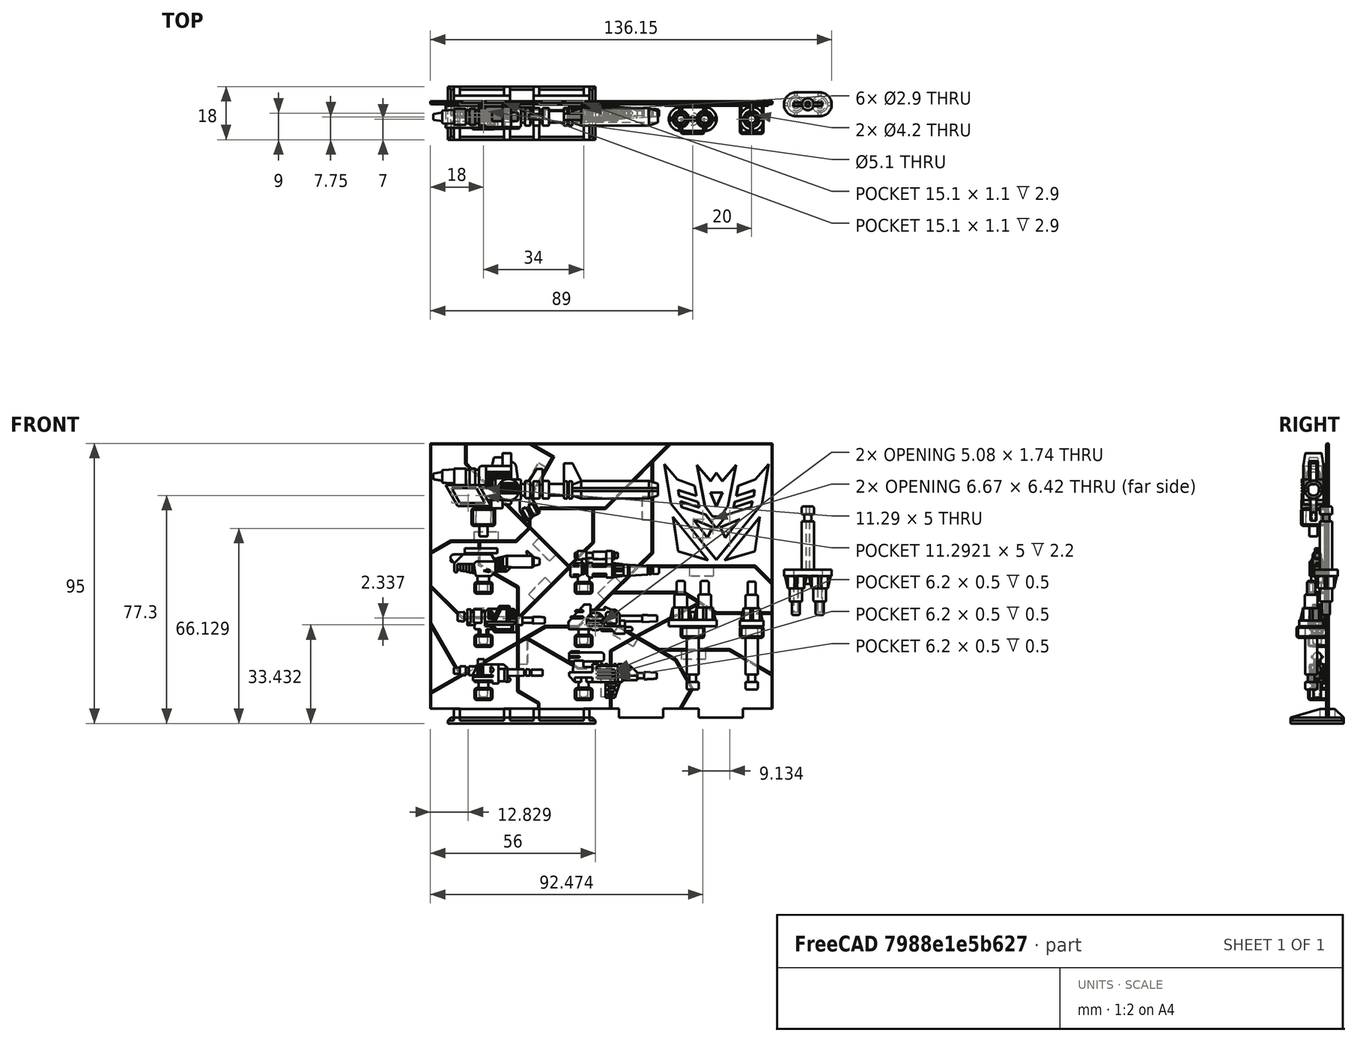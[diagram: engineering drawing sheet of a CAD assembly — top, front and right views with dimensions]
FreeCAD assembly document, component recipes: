
FREECAD ASSEMBLY — COMPONENT RECIPES ("Accesories")

This assembly document has 10 components, labeled P0..P9 below (a component is one placed body or linked part). 9 of them carry a construction recipe — the FreeCAD feature program that regenerates the part from scratch, quoted from this document or its linked companion documents; the rest are supplied as boundary geometry only. No exploded tour is included for this assembly.
NOTE — document 3 of 3 of this assembly tour. The two overview renders and the header above are repeated from document 1; the component sections below continue where the previous document stopped.
COMPONENT P8 — recipe-attached ("Scavanger_Gun", modeled in this document).
Construction recipe (the document's own serialized feature program — sketch geometry with constraints, then the solid features built on it; lengths are millimeters unless a unit is written):

FEATURE [Sketcher::SketchObject] Sketch357
  ArcFitTolerance = 1e-06
  AttachmentOffset = pos=(-22,-37,0) rot=(0,0,1;0rad)
  AttachmentSupport = -> [XZ_Plane027]
  FullyConstrained = true
  MakeInternals = false
  MapMode = 5
  Placement = pos=(-22,-8.2e-15,-37) rot=(1,0,0;1.5708rad)
  sketch-geometry (5):
    g0: LineSegment StartX=-1.6 StartY=-3 StartZ=0 EndX=7 EndY=-3 EndZ=0
    g1: LineSegment StartX=7 StartY=-3 StartZ=0 EndX=7 EndY=3.5 EndZ=0
    g2: LineSegment StartX=7 StartY=3.5 StartZ=0 EndX=0 EndY=3.5 EndZ=0
    g3: LineSegment StartX=0 StartY=3.5 StartZ=0 EndX=-1.6 EndY=0 EndZ=0
    g4: LineSegment StartX=-1.6 StartY=0 StartZ=0 EndX=-1.6 EndY=-3 EndZ=0
  constraints (15):
    c: Horizontal(g0)
    c: Coincident(g1,g0)
    c: Vertical(g1)
    c: Coincident(g2,g1)
    c: Horizontal(g2)
    c: Coincident(g3,g2)
    c: Coincident(g4,g3)
    c: Vertical(g4)
    c: Coincident(g0,g4)
    c: DistanceX(g0,g0) = 8.6
    c: PointOnObject(g2,g-2)
    c: DistanceY(g1,g1) = 6.5
    c: DistanceX(g2,g2) = 7
    c: DistanceY(g4,g4) = 3
    c: PointOnObject(g3,g-1)
FEATURE [PartDesign::Pad] Pad234
  Direction = (0,-1,2e-16)
  Length = 5
  Length2 = 10
  Placement = pos=(0,0,0) rot=(1,0,0;1.5708rad)
  Profile = -> Sketch357
  ReferenceAxis = -> Sketch357 [N_Axis]
  Refine = true
  Suppressed = false
  Type = 0
FEATURE [Sketcher::SketchObject] Sketch358
  ArcFitTolerance = 1e-06
  AttachmentSupport = -> [Pad234]
  ExternalGeometry = -> [Pad234]
  FullyConstrained = true
  MakeInternals = false
  MapMode = 5
  Placement = pos=(0,-1.76e-14,-40) rot=(1,0,0;3.14159rad)
  sketch-geometry (8):
    g0: LineSegment StartX=-17.1 StartY=5 StartZ=0 EndX=-17.1 EndY=4.5 EndZ=0
    g1: LineSegment StartX=-17.1 StartY=4.5 StartZ=0 EndX=-23.1 EndY=4.5 EndZ=0
    g2: LineSegment StartX=-23.1 StartY=4.5 StartZ=0 EndX=-23.1 EndY=0.5 EndZ=0
    g3: LineSegment StartX=-23.1 StartY=0.5 StartZ=0 EndX=-17.1 EndY=0.5 EndZ=0
    g4: LineSegment StartX=-17.1 StartY=0.5 StartZ=0 EndX=-17.1 EndY=0 EndZ=0
    g5: LineSegment StartX=-17.1 StartY=0 StartZ=0 EndX=-23.6 EndY=0 EndZ=0
    g6: LineSegment StartX=-23.6 StartY=0 StartZ=0 EndX=-23.6 EndY=5 EndZ=0
    g7: LineSegment StartX=-23.6 StartY=5 StartZ=0 EndX=-17.1 EndY=5 EndZ=0
  constraints (22):
    c: PointOnObject(g0,g-3)
    c: Vertical(g0)
    c: Coincident(g1,g0)
    c: Horizontal(g1)
    c: Coincident(g2,g1)
    c: Vertical(g2)
    c: Coincident(g3,g2)
    c: Horizontal(g3)
    c: Coincident(g4,g3)
    c: PointOnObject(g4,g-4)
    c: Vertical(g4)
    c: Coincident(g5,g4)
    c: Coincident(g5,g-5)
    c: Coincident(g6,g5)
    c: Coincident(g6,g-5)
    c: Coincident(g7,g6)
    c: Coincident(g7,g0)
    c: DistanceY(g0,g0) = 0.5
    c: DistanceY(g4,g4) = 0.5
    c: DistanceX(g6,g1) = 0.5
    c: DistanceX(g0,g-3) = 2.1
    c: DistanceX(g4,g-4) = 2.1
FEATURE [PartDesign::Pocket] Pocket060
  BaseFeature = -> Pad234
  Direction = (0,0,1)
  Length = 1
  Length2 = 5
  Placement = pos=(0,0,0) rot=(1,0,0;1.5708rad)
  Profile = -> Sketch358
  ReferenceAxis = -> Sketch358 [N_Axis]
  Refine = true
  Suppressed = false
  Type = 0
FEATURE [Sketcher::SketchObject] Sketch359
  ArcFitTolerance = 1e-06
  AttachmentSupport = -> [Pocket060]
  ExternalGeometry = -> [Pocket060]
  FullyConstrained = true
  MakeInternals = false
  MapMode = 5
  Placement = pos=(0,-1.76e-14,-40) rot=(1,0,0;3.14159rad)
  sketch-geometry (4):
    g0: LineSegment StartX=-23.1 StartY=4.5 StartZ=0 EndX=-23.1 EndY=0.5 EndZ=0
    g1: LineSegment StartX=-23.1 StartY=0.5 StartZ=0 EndX=-17.1 EndY=0.5 EndZ=0
    g2: LineSegment StartX=-17.1 StartY=0.5 StartZ=0 EndX=-17.1 EndY=4.5 EndZ=0
    g3: LineSegment StartX=-17.1 StartY=4.5 StartZ=0 EndX=-23.1 EndY=4.5 EndZ=0
  constraints (10):
    c: Coincident(g0,g1)
    c: Coincident(g1,g2)
    c: Coincident(g2,g3)
    c: Coincident(g3,g0)
    c: Vertical(g0)
    c: Vertical(g2)
    c: Horizontal(g1)
    c: Horizontal(g3)
    c: Coincident(g0,g-3)
    c: Coincident(g1,g-4)
FEATURE [PartDesign::Pocket] Pocket061
  BaseFeature = -> Pocket060
  Direction = (0,0,1)
  Length = 0.5
  Length2 = 5
  Placement = pos=(0,0,0) rot=(1,0,0;1.5708rad)
  Profile = -> Sketch359
  ReferenceAxis = -> Sketch359 [N_Axis]
  Refine = true
  Suppressed = false
  Type = 0
FEATURE [Sketcher::SketchObject] Sketch360
  ArcFitTolerance = 1e-06
  AttachmentSupport = -> [Pocket061]
  ExternalGeometry = -> [Pocket061]
  FullyConstrained = true
  MakeInternals = false
  MapMode = 5
  Placement = pos=(0,0,-39.5) rot=(1,0,0;3.14159rad)
  sketch-geometry (1):
    g0: Circle CenterX=-20.1 CenterY=2.5 CenterZ=0 NormalX=0 NormalY=0 NormalZ=1 AngleXU=0 Radius=1.7
  constraints (5):
    c: Radius(g0) = 1.7
    c: DistanceX(g-3,g-3) = 6
    c: DistanceY(g-5,g-5) = 4
    c: DistanceY(g0,g-5) = 2
    c: DistanceX(g-5,g0) = 3
FEATURE [PartDesign::Pad] Pad235
  BaseFeature = -> Pocket061
  Direction = (0,0,-1)
  Length = 2
  Length2 = 10
  Placement = pos=(0,0,0) rot=(1,0,0;1.5708rad)
  Profile = -> Sketch360
  ReferenceAxis = -> Sketch360 [N_Axis]
  Refine = true
  Suppressed = false
  Type = 0
FEATURE [Sketcher::SketchObject] Sketch361
  ArcFitTolerance = 1e-06
  AttachmentSupport = -> [Pad235]
  ExternalGeometry = -> [Pad235]
  FullyConstrained = true
  MakeInternals = false
  MapMode = 5
  Placement = pos=(0,0,-41.5) rot=(1,0,0;3.14159rad)
  sketch-geometry (1):
    g0: Circle CenterX=-20.1 CenterY=2.5 CenterZ=0 NormalX=0 NormalY=0 NormalZ=1 AngleXU=0 Radius=1.4
  constraints (2):
    c: Coincident(g0,g-3)
    c: Radius(g0) = 1.4
FEATURE [PartDesign::Pad] Pad236
  BaseFeature = -> Pad235
  Direction = (0,0,-1)
  Length = 3.1
  Length2 = 10
  Placement = pos=(0,0,0) rot=(1,0,0;1.5708rad)
  Profile = -> Sketch361
  ReferenceAxis = -> Sketch361 [N_Axis]
  Refine = true
  Suppressed = false
  Type = 0
FEATURE [PartDesign::Fillet] Fillet046
  Base = -> Pad236 [Edge39]
  BaseFeature = -> Pad236
  Placement = pos=(0,0,0) rot=(1,0,0;1.5708rad)
  Radius = 1
  Refine = true
  SupportTransform = false
  Suppressed = false
  UseAllEdges = false
FEATURE [Sketcher::SketchObject] Sketch362
  ArcFitTolerance = 1e-06
  AttachmentSupport = -> [Fillet046]
  ExternalGeometry = -> [Fillet046]
  FullyConstrained = true
  MakeInternals = false
  MapMode = 5
  Placement = pos=(0,-5,0) rot=(1,0,0;1.5708rad)
  sketch-geometry (7):
    g0: LineSegment StartX=-23.6 StartY=-37.7 StartZ=0 EndX=-17.1 EndY=-37.7 EndZ=0
    g1: ArcOfCircle CenterX=-17.1 CenterY=-37.45 CenterZ=0 NormalX=0 NormalY=0 NormalZ=1 AngleXU=0 Radius=0.25 StartAngle=4.71239 EndAngle=7.85398
    g2: LineSegment StartX=-17.1 StartY=-37.2 StartZ=0 EndX=-23.6 EndY=-37.2 EndZ=0
    g3: LineSegment StartX=-23.6 StartY=-37.2 StartZ=0 EndX=-23.6 EndY=-37.7 EndZ=0
    g4: LineSegment [constr] StartX=-17.1 StartY=-37.7 StartZ=0 EndX=-17.1 EndY=-39 EndZ=0
    g5: LineSegment [constr] StartX=-17.1 StartY=-37.2 StartZ=0 EndX=-17.1 EndY=-37.45 EndZ=0
    g6: LineSegment [constr] StartX=-17.1 StartY=-37.45 StartZ=0 EndX=-17.1 EndY=-37.7 EndZ=0
  constraints (19):
    c: PointOnObject(g0,g-5)
    c: Horizontal(g0)
    c: Coincident(g1,g0)
    c: Coincident(g2,g1)
    c: PointOnObject(g2,g-5)
    c: Horizontal(g2)
    c: Coincident(g3,g2)
    c: Coincident(g3,g0)
    c: DistanceY(g3,g3) = 0.5
    c: DistanceY(g-5,g0) = 1.3
    c: Coincident(g4,g0)
    c: Coincident(g4,g-4)
    c: Vertical(g4)
    c: Coincident(g5,g1)
    c: Coincident(g5,g1)
    c: Coincident(g6,g1)
    c: Coincident(g6,g0)
    c: Vertical(g5)
    c: Vertical(g6)
FEATURE [PartDesign::Pocket] Pocket062
  BaseFeature = -> Fillet046
  Direction = (0,1,-2e-16)
  Length = 0.5
  Length2 = 5
  Placement = pos=(0,0,0) rot=(1,0,0;1.5708rad)
  Profile = -> Sketch362
  ReferenceAxis = -> Sketch362 [N_Axis]
  Refine = true
  Suppressed = false
  Type = 0
FEATURE [Sketcher::SketchObject] Sketch363
  ArcFitTolerance = 1e-06
  AttachmentSupport = -> [Pocket062]
  ExternalGeometry = -> [Pocket062]
  FullyConstrained = true
  MakeInternals = false
  MapMode = 5
  Placement = pos=(-23.6,0,0) rot=(0.707107,0,-0.707107;3.14159rad)
  sketch-geometry (4):
    g0: LineSegment StartX=37.2 StartY=4.5 StartZ=0 EndX=37.2 EndY=8e-15 EndZ=0
    g1: LineSegment StartX=37.2 StartY=8.4e-15 StartZ=0 EndX=37.7 EndY=8.4e-15 EndZ=0
    g2: LineSegment StartX=37.7 StartY=8.4e-15 StartZ=0 EndX=37.7 EndY=4.5 EndZ=0
    g3: LineSegment StartX=37.7 StartY=4.5 StartZ=0 EndX=37.2 EndY=4.5 EndZ=0
  constraints (10):
    c: Coincident(g0,g1)
    c: Coincident(g1,g2)
    c: Coincident(g2,g3)
    c: Coincident(g3,g0)
    c: Vertical(g0)
    c: Vertical(g2)
    c: Horizontal(g1)
    c: Coincident(g0,g-4)
    c: PointOnObject(g1,g-3)
    c: Coincident(g2,g-4)
FEATURE [PartDesign::Pocket] Pocket063
  BaseFeature = -> Pocket062
  Direction = (1,0,2e-16)
  Length = 0.5
  Length2 = 5
  Placement = pos=(0,0,0) rot=(1,0,0;1.5708rad)
  Profile = -> Sketch363
  ReferenceAxis = -> Sketch363 [N_Axis]
  Refine = true
  Suppressed = false
  Type = 0
FEATURE [Sketcher::SketchObject] Sketch364
  ArcFitTolerance = 1e-06
  AttachmentSupport = -> [Pocket063]
  ExternalGeometry = -> [Pocket063]
  FullyConstrained = false
  MakeInternals = false
  MapMode = 5
  Placement = pos=(0,-8.2e-15,0) rot=(-1,0,0;1.5708rad)
  sketch-geometry (4):
    g0: LineSegment StartX=-23.1 StartY=37.7 StartZ=0 EndX=-23.1 EndY=37.2 EndZ=0
    g1: LineSegment StartX=-23.1 StartY=37.2 StartZ=0 EndX=-17.1 EndY=37.2 EndZ=0
    g2: LineSegment StartX=-17.1 StartY=37.7 StartZ=0 EndX=-23.1 EndY=37.7 EndZ=0
    g3: ArcOfCircle CenterX=-17.1 CenterY=37.45 CenterZ=0 NormalX=0 NormalY=0 NormalZ=1 AngleXU=0 Radius=0.25 StartAngle=4.71239 EndAngle=7.85398
  constraints (8):
    c: Coincident(g0,g-6)
    c: Coincident(g0,g-6)
    c: Coincident(g1,g0)
    c: Coincident(g1,g-5)
    c: Coincident(g2,g-4)
    c: Coincident(g2,g0)
    c: Coincident(g3,g2)
    c: Coincident(g3,g1)
FEATURE [PartDesign::Pocket] Pocket064
  BaseFeature = -> Pocket063
  Direction = (0,-1,-2e-16)
  Length = 0.5
  Length2 = 5
  Placement = pos=(0,0,0) rot=(1,0,0;1.5708rad)
  Profile = -> Sketch364
  ReferenceAxis = -> Sketch364 [N_Axis]
  Refine = true
  Suppressed = false
  Type = 0
FEATURE [Sketcher::SketchObject] Sketch365
  ArcFitTolerance = 1e-06
  AttachmentSupport = -> [Pocket064]
  ExternalGeometry = -> [Pocket064]
  FullyConstrained = true
  MakeInternals = false
  MapMode = 5
  Placement = pos=(0,-8.2e-15,0) rot=(-1,0,0;1.5708rad)
  sketch-geometry (50):
    g0: LineSegment StartX=-20.2 StartY=34.1 StartZ=0 EndX=-20.2 EndY=36.6 EndZ=0
    g1: LineSegment StartX=-20.4 StartY=36.8 StartZ=0 EndX=-21.9 EndY=36.8 EndZ=0
    g2: LineSegment StartX=-22.1 StartY=36.6 StartZ=0 EndX=-22.1 EndY=34.1 EndZ=0
    g3: LineSegment StartX=-21.9 StartY=33.9 StartZ=0 EndX=-20.4 EndY=33.9 EndZ=0
    g4: ArcOfCircle CenterX=-20.4 CenterY=36.6 CenterZ=0 NormalX=0 NormalY=0 NormalZ=1 AngleXU=0 Radius=0.2 StartAngle=6e-16 EndAngle=1.5708
    g5: GeomPoint [constr] X=-20.2 Y=36.8 Z=0
    g6: ArcOfCircle CenterX=-21.9 CenterY=36.6 CenterZ=0 NormalX=0 NormalY=0 NormalZ=1 AngleXU=0 Radius=0.2 StartAngle=1.5708 EndAngle=3.14159
    g7: GeomPoint [constr] X=-22.1 Y=36.8 Z=0
    g8: ArcOfCircle CenterX=-21.9 CenterY=34.1 CenterZ=0 NormalX=0 NormalY=0 NormalZ=1 AngleXU=0 Radius=0.2 StartAngle=3.14159 EndAngle=4.71239
    g9: GeomPoint [constr] X=-22.1 Y=33.9 Z=0
    g10: ArcOfCircle CenterX=-20.4 CenterY=34.1 CenterZ=0 NormalX=0 NormalY=0 NormalZ=1 AngleXU=0 Radius=0.2 StartAngle=4.71239 EndAngle=6.28319
    g11: GeomPoint [constr] X=-20.2 Y=33.9 Z=0
    g12: LineSegment StartX=-20.4 StartY=34.28 StartZ=0 EndX=-20.4 EndY=34.68 EndZ=0
    g13: LineSegment StartX=-20.5 StartY=34.78 StartZ=0 EndX=-21.8 EndY=34.78 EndZ=0
    g14: LineSegment StartX=-21.9 StartY=34.68 StartZ=0 EndX=-21.9 EndY=34.28 EndZ=0
    g15: LineSegment StartX=-21.8 StartY=34.18 StartZ=0 EndX=-20.5 EndY=34.18 EndZ=0
    g16: ArcOfCircle CenterX=-21.8 CenterY=34.68 CenterZ=0 NormalX=0 NormalY=0 NormalZ=1 AngleXU=0 Radius=0.1 StartAngle=1.5708 EndAngle=3.14159
    g17: GeomPoint [constr] X=-21.9 Y=34.78 Z=0
    g18: ArcOfCircle CenterX=-21.8 CenterY=34.28 CenterZ=0 NormalX=0 NormalY=0 NormalZ=1 AngleXU=0 Radius=0.1 StartAngle=3.14159 EndAngle=4.71239
    g19: GeomPoint [constr] X=-21.9 Y=34.18 Z=0
    g20: ArcOfCircle CenterX=-20.5 CenterY=34.68 CenterZ=0 NormalX=0 NormalY=0 NormalZ=1 AngleXU=0 Radius=0.1 StartAngle=4.6e-15 EndAngle=1.5708
    g21: GeomPoint [constr] X=-20.4 Y=34.78 Z=0
    g22: ArcOfCircle CenterX=-20.5 CenterY=34.28 CenterZ=0 NormalX=0 NormalY=0 NormalZ=1 AngleXU=0 Radius=0.1 StartAngle=4.71239 EndAngle=6.28319
    g23: GeomPoint [constr] X=-20.4 Y=34.18 Z=0
    g24: LineSegment StartX=-20.4 StartY=35.15 StartZ=0 EndX=-20.4 EndY=35.55 EndZ=0
    g25: LineSegment StartX=-20.5 StartY=35.65 StartZ=0 EndX=-21.8 EndY=35.65 EndZ=0
    g26: LineSegment StartX=-21.9 StartY=35.55 StartZ=0 EndX=-21.9 EndY=35.15 EndZ=0
    g27: LineSegment StartX=-21.8 StartY=35.05 StartZ=0 EndX=-20.5 EndY=35.05 EndZ=0
    g28: LineSegment StartX=-20.4 StartY=36.02 StartZ=0 EndX=-20.4 EndY=36.42 EndZ=0
    g29: LineSegment StartX=-20.5 StartY=36.52 StartZ=0 EndX=-21.8 EndY=36.52 EndZ=0
    g30: LineSegment StartX=-21.9 StartY=36.42 StartZ=0 EndX=-21.9 EndY=36.02 EndZ=0
    g31: LineSegment StartX=-21.8 StartY=35.92 StartZ=0 EndX=-20.5 EndY=35.92 EndZ=0
    g32: ArcOfCircle CenterX=-20.5 CenterY=35.15 CenterZ=0 NormalX=0 NormalY=0 NormalZ=1 AngleXU=0 Radius=0.1 StartAngle=4.71239 EndAngle=6.28319
    g33: GeomPoint [constr] X=-20.4 Y=35.05 Z=0
    g34: ArcOfCircle CenterX=-21.8 CenterY=35.15 CenterZ=0 NormalX=0 NormalY=0 NormalZ=1 AngleXU=0 Radius=0.1 StartAngle=3.14159 EndAngle=4.71239
    g35: GeomPoint [constr] X=-21.9 Y=35.05 Z=0
    g36: ArcOfCircle CenterX=-21.8 CenterY=35.55 CenterZ=0 NormalX=0 NormalY=0 NormalZ=1 AngleXU=0 Radius=0.1 StartAngle=1.5708 EndAngle=3.14159
    g37: GeomPoint [constr] X=-21.9 Y=35.65 Z=0
    g38: ArcOfCircle CenterX=-20.5 CenterY=35.55 CenterZ=0 NormalX=0 NormalY=0 NormalZ=1 AngleXU=0 Radius=0.1 StartAngle=-9e-16 EndAngle=1.5708
    g39: GeomPoint [constr] X=-20.4 Y=35.65 Z=0
    g40: ArcOfCircle CenterX=-20.5 CenterY=36.02 CenterZ=0 NormalX=0 NormalY=0 NormalZ=1 AngleXU=0 Radius=0.1 StartAngle=4.71239 EndAngle=6.28319
    g41: GeomPoint [constr] X=-20.4 Y=35.92 Z=0
    g42: ArcOfCircle CenterX=-20.5 CenterY=36.42 CenterZ=0 NormalX=0 NormalY=0 NormalZ=1 AngleXU=0 Radius=0.1 StartAngle=1e-16 EndAngle=1.5708
    g43: GeomPoint [constr] X=-20.4 Y=36.52 Z=0
    g44: ArcOfCircle CenterX=-21.8 CenterY=36.42 CenterZ=0 NormalX=0 NormalY=0 NormalZ=1 AngleXU=0 Radius=0.1 StartAngle=1.5708 EndAngle=3.14159
    g45: GeomPoint [constr] X=-21.9 Y=36.52 Z=0
    g46: ArcOfCircle CenterX=-21.8 CenterY=36.02 CenterZ=0 NormalX=0 NormalY=0 NormalZ=1 AngleXU=0 Radius=0.1 StartAngle=3.14159 EndAngle=4.71239
    g47: GeomPoint [constr] X=-21.9 Y=35.92 Z=0
    g48: LineSegment [constr] StartX=-20.5 StartY=34.78 StartZ=0 EndX=-20.5 EndY=35.05 EndZ=0
    g49: LineSegment [constr] StartX=-20.5 StartY=35.65 StartZ=0 EndX=-20.5 EndY=35.92 EndZ=0
  constraints (118):
    c: Vertical(g0)
    c: Vertical(g2)
    c: Horizontal(g1)
    c: Horizontal(g3)
    c: PointOnObject(g5,g0)
    c: PointOnObject(g5,g1)
    c: Tangent(g0,g4) = -1.5708
    c: Tangent(g1,g4) = -1.5708
    c: PointOnObject(g7,g1)
    c: PointOnObject(g7,g2)
    c: Tangent(g1,g6) = -1.5708
    c: Tangent(g2,g6) = -1.5708
    c: PointOnObject(g9,g2)
    c: PointOnObject(g9,g3)
    c: Tangent(g2,g8) = -1.5708
    c: Tangent(g3,g8) = -1.5708
    c: PointOnObject(g11,g0)
    c: PointOnObject(g11,g3)
    c: Tangent(g0,g10) = -1.5708
    c: Tangent(g3,g10) = -1.5708
    c: Radius(g4) = 0.2
    c: Radius(g6) = 0.2
    c: Radius(g8) = 0.2
    c: Radius(g10) = 0.2
    c: DistanceX(g2,g0) = 1.9
    c: DistanceY(g3,g1) = 2.9
    c: DistanceY(g-3,g3) = 0.4
    c: DistanceY(g1,g-4) = 0.4
    c: DistanceX(g-5,g1) = 1.7
    c: Vertical(g12)
    c: Vertical(g14)
    c: Horizontal(g13)
    c: Horizontal(g15)
    c: PointOnObject(g17,g13)
    c: PointOnObject(g17,g14)
    c: Tangent(g13,g16) = -1.5708
    c: Tangent(g14,g16) = -1.5708
    c: PointOnObject(g19,g14)
    c: PointOnObject(g19,g15)
    c: Tangent(g14,g18) = -1.5708
    c: Tangent(g15,g18) = -1.5708
    c: PointOnObject(g21,g12)
    c: PointOnObject(g21,g13)
    c: Tangent(g12,g20) = -1.5708
    c: Tangent(g13,g20) = -1.5708
    c: PointOnObject(g23,g12)
    c: PointOnObject(g23,g15)
    c: Tangent(g12,g22) = -1.5708
    c: Tangent(g15,g22) = -1.5708
    c: Radius(g20) = 0.1
    c: Radius(g22) = 0.1
    c: Radius(g16) = 0.1
    c: Radius(g18) = 0.1
    c: DistanceX(g14,g12) = 1.5
    c: Vertical(g24)
    c: Vertical(g26)
    c: Horizontal(g25)
    c: Horizontal(g27)
    c: Vertical(g28)
    c: Vertical(g30)
    c: Horizontal(g29)
    c: Horizontal(g31)
    c: PointOnObject(g33,g24)
    c: PointOnObject(g33,g27)
    c: Tangent(g24,g32) = -1.5708
    c: Tangent(g27,g32) = -1.5708
    c: PointOnObject(g35,g26)
    c: PointOnObject(g35,g27)
    c: Tangent(g26,g34) = -1.5708
    c: Tangent(g27,g34) = -1.5708
    c: PointOnObject(g37,g25)
    c: PointOnObject(g37,g26)
    c: Tangent(g25,g36) = -1.5708
    c: Tangent(g26,g36) = -1.5708
    c: PointOnObject(g39,g24)
    c: PointOnObject(g39,g25)
    c: Tangent(g24,g38) = -1.5708
    c: Tangent(g25,g38) = -1.5708
    c: PointOnObject(g41,g28)
    c: PointOnObject(g41,g31)
    c: Tangent(g28,g40) = -1.5708
    c: Tangent(g31,g40) = -1.5708
    c: PointOnObject(g43,g28)
    c: PointOnObject(g43,g29)
    c: Tangent(g28,g42) = -1.5708
    c: Tangent(g29,g42) = -1.5708
    c: PointOnObject(g45,g29)
    c: PointOnObject(g45,g30)
    c: Tangent(g29,g44) = -1.5708
    c: Tangent(g30,g44) = -1.5708
    c: PointOnObject(g47,g30)
    c: PointOnObject(g47,g31)
    c: Tangent(g30,g46) = -1.5708
    c: Tangent(g31,g46) = -1.5708
    c: Radius(g32) = 0.1
    c: Radius(g38) = 0.1
    c: Radius(g34) = 0.1
    c: Radius(g36) = 0.1
    c: DistanceX(g26,g24) = 1.5
    c: Radius(g40) = 0.1
    c: Radius(g46) = 0.1
    c: Radius(g44) = 0.1
    c: Radius(g42) = 0.1
    c: DistanceX(g30,g28) = 1.5
    c: DistanceY(g15,g13) = 0.6
    c: DistanceY(g27,g25) = 0.6
    c: DistanceY(g31,g29) = 0.6
    c: DistanceX(g12,g0) = 0.2
    c: Coincident(g48,g13)
    c: Coincident(g48,g27)
    c: Coincident(g49,g25)
    c: Coincident(g49,g31)
    c: Vertical(g49)
    c: Vertical(g48)
    c: DistanceY(g3,g15) = 0.28
    c: DistanceY(g48,g48) = 0.27
    c: DistanceY(g49,g49) = 0.27
    c: DistanceY(g29,g1) = 0.28
FEATURE [PartDesign::Pocket] Pocket065
  BaseFeature = -> Pocket064
  Direction = (0,-1,-2e-16)
  Length = 0.5
  Length2 = 5
  Placement = pos=(0,0,0) rot=(1,0,0;1.5708rad)
  Profile = -> Sketch365
  ReferenceAxis = -> Sketch365 [N_Axis]
  Refine = true
  Suppressed = false
  Type = 0
FEATURE [Sketcher::SketchObject] Sketch366
  ArcFitTolerance = 1e-06
  AttachmentSupport = -> [Pocket065]
  ExternalGeometry = -> [Pocket065]
  FullyConstrained = true
  MakeInternals = false
  MapMode = 5
  Placement = pos=(0,-5,0) rot=(1,0,0;1.5708rad)
  sketch-geometry (32):
    g0: LineSegment StartX=-21.8 StartY=-34.18 StartZ=0 EndX=-20.5 EndY=-34.18 EndZ=0
    g1: LineSegment StartX=-20.5 StartY=-34.78 StartZ=0 EndX=-21.8 EndY=-34.78 EndZ=0
    g2: LineSegment StartX=-21.9 StartY=-34.28 StartZ=0 EndX=-21.9 EndY=-34.68 EndZ=0
    g3: LineSegment StartX=-20.4 StartY=-34.28 StartZ=0 EndX=-20.4 EndY=-34.68 EndZ=0
    g4: LineSegment StartX=-20.2 StartY=-34.1 StartZ=0 EndX=-20.2 EndY=-36.6 EndZ=0
    g5: LineSegment StartX=-20.4 StartY=-36.8 StartZ=0 EndX=-21.9 EndY=-36.8 EndZ=0
    g6: LineSegment StartX=-22.1 StartY=-36.6 StartZ=0 EndX=-22.1 EndY=-34.1 EndZ=0
    g7: LineSegment StartX=-21.9 StartY=-33.9 StartZ=0 EndX=-20.4 EndY=-33.9 EndZ=0
    g8: LineSegment StartX=-20.5 StartY=-35.05 StartZ=0 EndX=-21.8 EndY=-35.05 EndZ=0
    g9: LineSegment StartX=-21.9 StartY=-35.15 StartZ=0 EndX=-21.9 EndY=-35.55 EndZ=0
    g10: LineSegment StartX=-21.8 StartY=-35.65 StartZ=0 EndX=-20.5 EndY=-35.65 EndZ=0
    g11: LineSegment StartX=-20.4 StartY=-35.55 StartZ=0 EndX=-20.4 EndY=-35.15 EndZ=0
    g12: LineSegment StartX=-21.9 StartY=-36.02 StartZ=0 EndX=-21.9 EndY=-36.42 EndZ=0
    g13: LineSegment StartX=-21.8 StartY=-36.52 StartZ=0 EndX=-20.5 EndY=-36.52 EndZ=0
    g14: LineSegment StartX=-20.4 StartY=-36.42 StartZ=0 EndX=-20.4 EndY=-36.02 EndZ=0
    g15: LineSegment StartX=-20.5 StartY=-35.92 StartZ=0 EndX=-21.8 EndY=-35.92 EndZ=0
    g16: ArcOfCircle CenterX=-21.8 CenterY=-35.55 CenterZ=0 NormalX=0 NormalY=0 NormalZ=1 AngleXU=0 Radius=0.0999981 StartAngle=3.14157 EndAngle=4.71241
    g17: ArcOfCircle CenterX=-20.5 CenterY=-35.55 CenterZ=0 NormalX=0 NormalY=0 NormalZ=1 AngleXU=0 Radius=0.0999969 StartAngle=4.71236 EndAngle=6.28322
    g18: ArcOfCircle CenterX=-20.5 CenterY=-35.15 CenterZ=0 NormalX=0 NormalY=0 NormalZ=1 AngleXU=0 Radius=0.0999972 StartAngle=6.28316 EndAngle=7.85401
    g19: ArcOfCircle CenterX=-21.8 CenterY=-35.15 CenterZ=0 NormalX=0 NormalY=0 NormalZ=1 AngleXU=0 Radius=0.0999984 StartAngle=1.57078 EndAngle=3.14161
    g20: ArcOfCircle CenterX=-21.8 CenterY=-34.68 CenterZ=0 NormalX=0 NormalY=0 NormalZ=1 AngleXU=0 Radius=0.0999981 StartAngle=3.14157 EndAngle=4.71241
    g21: ArcOfCircle CenterX=-21.8 CenterY=-34.28 CenterZ=0 NormalX=0 NormalY=0 NormalZ=1 AngleXU=0 Radius=0.0999975 StartAngle=1.57077 EndAngle=3.14162
    g22: ArcOfCircle CenterX=-20.5 CenterY=-34.28 CenterZ=0 NormalX=0 NormalY=0 NormalZ=1 AngleXU=0 Radius=0.099998 StartAngle=6.28316 EndAngle=7.854
    g23: ArcOfCircle CenterX=-20.5 CenterY=-34.68 CenterZ=0 NormalX=0 NormalY=0 NormalZ=1 AngleXU=0 Radius=0.0999979 StartAngle=4.71237 EndAngle=6.28321
    g24: ArcOfCircle CenterX=-20.4 CenterY=-34.1 CenterZ=0 NormalX=0 NormalY=0 NormalZ=1 AngleXU=0 Radius=0.199996 StartAngle=6.28317 EndAngle=7.854
    g25: ArcOfCircle CenterX=-21.9 CenterY=-34.1 CenterZ=0 NormalX=0 NormalY=0 NormalZ=1 AngleXU=0 Radius=0.2 StartAngle=1.5708 EndAngle=3.14159
    g26: ArcOfCircle CenterX=-21.8 CenterY=-36.02 CenterZ=0 NormalX=0 NormalY=0 NormalZ=1 AngleXU=0 Radius=0.099998 StartAngle=1.57078 EndAngle=3.14161
    g27: ArcOfCircle CenterX=-20.5 CenterY=-36.02 CenterZ=0 NormalX=0 NormalY=0 NormalZ=1 AngleXU=0 Radius=0.0999979 StartAngle=6.28316 EndAngle=7.854
    g28: ArcOfCircle CenterX=-20.5 CenterY=-36.42 CenterZ=0 NormalX=0 NormalY=0 NormalZ=1 AngleXU=0 Radius=0.0999976 StartAngle=4.71237 EndAngle=6.28321
    g29: ArcOfCircle CenterX=-20.4 CenterY=-36.6 CenterZ=0 NormalX=0 NormalY=0 NormalZ=1 AngleXU=0 Radius=0.199996 StartAngle=4.71237 EndAngle=6.28321
    g30: ArcOfCircle CenterX=-21.9 CenterY=-36.6 CenterZ=0 NormalX=0 NormalY=0 NormalZ=1 AngleXU=0 Radius=0.199997 StartAngle=3.14158 EndAngle=4.7124
    g31: ArcOfCircle CenterX=-21.8 CenterY=-36.42 CenterZ=0 NormalX=0 NormalY=0 NormalZ=1 AngleXU=0 Radius=0.0999974 StartAngle=3.14157 EndAngle=4.71242
  constraints (79):
    c: Coincident(g0,g-35)
    c: Coincident(g0,g-17)
    c: Coincident(g1,g-18)
    c: Coincident(g1,g-13)
    c: Coincident(g2,g-35)
    c: Coincident(g2,g-14)
    c: Coincident(g3,g-17)
    c: Coincident(g3,g-18)
    c: Coincident(g4,g-5)
    c: Coincident(g4,g-6)
    c: Coincident(g5,g-7)
    c: Coincident(g5,g-8)
    c: Coincident(g6,g-9)
    c: Coincident(g6,g-10)
    c: Coincident(g7,g-10)
    c: Coincident(g7,g-4)
    c: Coincident(g8,g-25)
    c: Coincident(g8,g-23)
    c: Coincident(g14,g-34)
    c: Coincident(g14,g-33)
    c: Coincident(g15,g-32)
    c: Coincident(g15,g-31)
    c: Coincident(g13,g-34)
    c: Coincident(g13,g-29)
    c: Coincident(g12,g-31)
    c: Coincident(g12,g-30)
    c: Coincident(g10,g-21)
    c: Coincident(g9,g-22)
    c: Coincident(g9,g-23)
    c: Coincident(g10,g-26)
    c: Coincident(g11,g-26)
    c: Coincident(g11,g-25)
    c: Coincident(g16,g10)
    c: Coincident(g16,g9)
    c: Coincident(g17,g10)
    c: Coincident(g17,g11)
    c: Coincident(g18,g11)
    c: Coincident(g18,g8)
    c: Coincident(g19,g8)
    c: Coincident(g19,g9)
    c: Tangent(g19,g-23)
    c: Tangent(g17,g-26)
    c: Tangent(g18,g-25)
    c: Tangent(g16,g-21)
    c: Coincident(g20,g1)
    c: Coincident(g20,g2)
    c: Coincident(g21,g2)
    c: Coincident(g21,g0)
    c: Coincident(g22,g0)
    c: Coincident(g22,g3)
    c: Coincident(g23,g3)
    c: Coincident(g23,g1)
    c: Coincident(g24,g4)
    c: Coincident(g24,g7)
    c: Coincident(g25,g7)
    c: Tangent(g25,g-10) = -1.5708
    c: Tangent(g21,g-35)
    c: Tangent(g22,g-17)
    c: Tangent(g24,g-4)
    c: Tangent(g20,g-13)
    c: Tangent(g23,g-18)
    c: Coincident(g26,g15)
    c: Coincident(g26,g12)
    c: Coincident(g27,g15)
    c: Coincident(g27,g14)
    c: Coincident(g28,g14)
    c: Coincident(g28,g13)
    c: Coincident(g29,g4)
    c: Coincident(g29,g5)
    c: Coincident(g30,g5)
    c: Coincident(g30,g6)
    c: Coincident(g31,g13)
    c: Coincident(g31,g12)
    c: Tangent(g30,g-8)
    c: Tangent(g31,g-29)
    c: Tangent(g29,g-6)
    c: Tangent(g28,g-34)
    c: Tangent(g27,g-32)
    c: Tangent(g26,g-31)
FEATURE [PartDesign::Pocket] Pocket066
  BaseFeature = -> Pocket065
  Direction = (0,1,-2e-16)
  Length = 0.5
  Length2 = 5
  Placement = pos=(0,0,0) rot=(1,0,0;1.5708rad)
  Profile = -> Sketch366
  ReferenceAxis = -> Sketch366 [N_Axis]
  Refine = true
  Suppressed = false
  Type = 0
FEATURE [Sketcher::SketchObject] Sketch367
  ArcFitTolerance = 1e-06
  AttachmentSupport = -> [Pocket066]
  ExternalGeometry = -> [Pocket066]
  FullyConstrained = true
  MakeInternals = false
  MapMode = 5
  Placement = pos=(0,-5,0) rot=(1,0,0;1.5708rad)
  sketch-geometry (2):
    g0: LineSegment StartX=-17.7 StartY=-34.35 StartZ=0 EndX=-17.7 EndY=-36.35 EndZ=0
    g1: ArcOfCircle CenterX=-17.7 CenterY=-35.35 CenterZ=0 NormalX=0 NormalY=0 NormalZ=1 AngleXU=0 Radius=1 StartAngle=4.71239 EndAngle=7.85398
  constraints (8):
    c: Vertical(g0)
    c: Coincident(g1,g0)
    c: Coincident(g1,g0)
    c: PointOnObject(g1,g0)
    c: Diameter(g1) = 2
    c: DistanceY(g-3,g-4) = 3.7
    c: DistanceY(g-3,g1) = 1.85
    c: DistanceX(g-5,g0) = 2.5
FEATURE [PartDesign::Pocket] Pocket067
  BaseFeature = -> Pocket066
  Direction = (0,1,-2e-16)
  Length = 0.5
  Length2 = 5
  Placement = pos=(0,0,0) rot=(1,0,0;1.5708rad)
  Profile = -> Sketch367
  ReferenceAxis = -> Sketch367 [N_Axis]
  Refine = true
  Suppressed = false
  Type = 0
FEATURE [Sketcher::SketchObject] Sketch368
  ArcFitTolerance = 1e-06
  AttachmentSupport = -> [Pocket067]
  ExternalGeometry = -> [Pocket067]
  FullyConstrained = true
  MakeInternals = false
  MapMode = 5
  Placement = pos=(0,-8.2e-15,0) rot=(-1,0,0;1.5708rad)
  sketch-geometry (2):
    g0: LineSegment StartX=-17.7 StartY=36.35 StartZ=0 EndX=-17.7 EndY=34.35 EndZ=0
    g1: ArcOfCircle CenterX=-17.7 CenterY=35.35 CenterZ=0 NormalX=0 NormalY=0 NormalZ=1 AngleXU=0 Radius=1 StartAngle=4.71239 EndAngle=7.85398
  constraints (5):
    c: Coincident(g0,g-4)
    c: Coincident(g0,g-4)
    c: Coincident(g1,g0)
    c: Coincident(g1,g0)
    c: Tangent(g1,g-4)
FEATURE [PartDesign::Pocket] Pocket068
  BaseFeature = -> Pocket067
  Direction = (0,-1,-2e-16)
  Length = 0.5
  Length2 = 5
  Placement = pos=(0,0,0) rot=(1,0,0;1.5708rad)
  Profile = -> Sketch368
  ReferenceAxis = -> Sketch368 [N_Axis]
  Refine = true
  Suppressed = false
  Type = 0
FEATURE [Sketcher::SketchObject] Sketch369
  ArcFitTolerance = 1e-06
  AttachmentSupport = -> [Pocket068]
  ExternalGeometry = -> [Pocket068]
  FullyConstrained = true
  MakeInternals = false
  MapMode = 5
  Placement = pos=(-23.6,0,0) rot=(0.707107,0,-0.707107;3.14159rad)
  sketch-geometry (1):
    g0: Circle CenterX=35.7 CenterY=2.5 CenterZ=0 NormalX=0 NormalY=0 NormalZ=1 AngleXU=0 Radius=1.5
  constraints (4):
    c: Diameter(g0) = 3
    c: Tangent(g0,g-3)
    c: DistanceY(g-4,g-4) = 5
    c: DistanceY(g0,g-4) = 2.5
FEATURE [PartDesign::Pad] Pad237
  BaseFeature = -> Pocket068
  Direction = (-1,0,-2e-16)
  Length = 1.5
  Length2 = 10
  Placement = pos=(0,0,0) rot=(1,0,0;1.5708rad)
  Profile = -> Sketch369
  ReferenceAxis = -> Sketch369 [N_Axis]
  Refine = true
  Reversed = true
  Suppressed = false
  Type = 0
FEATURE [PartDesign::Pad] Pad238
  BaseFeature = -> Pad237
  Direction = (-1,0,-2e-16)
  Length = 1.5
  Length2 = 10
  Placement = pos=(0,0,0) rot=(1,0,0;1.5708rad)
  Profile = -> Sketch369
  ReferenceAxis = -> Sketch369 [N_Axis]
  Refine = true
  Suppressed = false
  Type = 0
FEATURE [Sketcher::SketchObject] Sketch370
  ArcFitTolerance = 1e-06
  AttachmentSupport = -> [Pad238]
  ExternalGeometry = -> [Pad238]
  FullyConstrained = true
  MakeInternals = false
  MapMode = 5
  Placement = pos=(-25.1,0,0) rot=(0.707107,0,-0.707107;3.14159rad)
  sketch-geometry (1):
    g0: Circle CenterX=35.7 CenterY=2.5 CenterZ=0 NormalX=0 NormalY=0 NormalZ=1 AngleXU=0 Radius=1
  constraints (2):
    c: Coincident(g0,g-3)
    c: Radius(g0) = 1
FEATURE [PartDesign::Pad] Pad239
  BaseFeature = -> Pad238
  Direction = (-1,0,-2e-16)
  Length = 1
  Length2 = 10
  Placement = pos=(0,0,0) rot=(1,0,0;1.5708rad)
  Profile = -> Sketch370
  ReferenceAxis = -> Sketch370 [N_Axis]
  Refine = true
  Suppressed = false
  Type = 0
FEATURE [Sketcher::SketchObject] Sketch371
  ArcFitTolerance = 1e-06
  AttachmentSupport = -> [Pad239]
  ExternalGeometry = -> [Pad239]
  FullyConstrained = true
  MakeInternals = false
  MapMode = 5
  Placement = pos=(-26.1,0,0) rot=(0.707107,0,-0.707107;3.14159rad)
  sketch-geometry (1):
    g0: Circle CenterX=35.7 CenterY=2.5 CenterZ=0 NormalX=0 NormalY=0 NormalZ=1 AngleXU=0 Radius=1.5
  constraints (2):
    c: Coincident(g0,g-3)
    c: Equal(g0,g-3)
FEATURE [PartDesign::Pad] Pad240
  BaseFeature = -> Pad239
  Direction = (-1,0,-2e-16)
  Length = 2
  Length2 = 10
  Placement = pos=(0,0,0) rot=(1,0,0;1.5708rad)
  Profile = -> Sketch371
  ReferenceAxis = -> Sketch371 [N_Axis]
  Refine = true
  Suppressed = false
  Type = 0
FEATURE [Sketcher::SketchObject] Sketch372
  ArcFitTolerance = 1e-06
  AttachmentSupport = -> [Pad240]
  ExternalGeometry = -> [Pad240]
  FullyConstrained = true
  MakeInternals = false
  MapMode = 5
  Placement = pos=(-28.1,0,0) rot=(0.707107,0,-0.707107;3.14159rad)
  sketch-geometry (1):
    g0: Circle CenterX=35.7 CenterY=2.5 CenterZ=0 NormalX=0 NormalY=0 NormalZ=1 AngleXU=0 Radius=1.1
  constraints (2):
    c: Coincident(g0,g-3)
    c: Diameter(g0) = 2.2
FEATURE [Sketcher::SketchObject] Sketch373
  ArcFitTolerance = 1e-06
  AttachmentOffset = pos=(0,0,2) rot=(0,0,1;0rad)
  AttachmentSupport = -> [Pad240]
  ExternalGeometry = -> [Pad240]
  FullyConstrained = true
  MakeInternals = false
  MapMode = 5
  Placement = pos=(-30.1,0,-4e-16) rot=(0.707107,0,-0.707107;3.14159rad)
  sketch-geometry (1):
    g0: Circle CenterX=35.7 CenterY=2.5 CenterZ=0 NormalX=0 NormalY=0 NormalZ=1 AngleXU=0 Radius=1
  constraints (2):
    c: Coincident(g0,g-3)
    c: Diameter(g0) = 2
FEATURE [PartDesign::AdditiveLoft] AdditiveLoft021
  BaseFeature = -> Pad240
  Closed = false
  Placement = pos=(0,0,0) rot=(1,0,0;1.5708rad)
  Profile = -> Sketch372
  Refine = true
  Ruled = false
  Sections = -> [Sketch373]
  Suppressed = false
FEATURE [Sketcher::SketchObject] Sketch374
  ArcFitTolerance = 1e-06
  AttachmentSupport = -> [AdditiveLoft021]
  ExternalGeometry = -> [AdditiveLoft021]
  FullyConstrained = true
  MakeInternals = false
  MapMode = 5
  Placement = pos=(0,-1.47e-14,-33.5) rot=(0,0,1;3.14159rad)
  sketch-geometry (4):
    g0: LineSegment StartX=15 StartY=3.85 StartZ=0 EndX=15 EndY=1.15 EndZ=0
    g1: LineSegment StartX=15 StartY=1.15 StartZ=0 EndX=17.2 EndY=1.15 EndZ=0
    g2: LineSegment StartX=17.2 StartY=1.15 StartZ=0 EndX=17.2 EndY=3.85 EndZ=0
    g3: LineSegment StartX=17.2 StartY=3.85 StartZ=0 EndX=15 EndY=3.85 EndZ=0
  constraints (13):
    c: Coincident(g0,g1)
    c: Coincident(g1,g2)
    c: Coincident(g2,g3)
    c: Coincident(g3,g0)
    c: Vertical(g0)
    c: Vertical(g2)
    c: Horizontal(g1)
    c: Horizontal(g3)
    c: PointOnObject(g0,g-5)
    c: DistanceY(g0,g0) = 2.7
    c: DistanceX(g3,g3) = 2.2
    c: DistanceY(g-5,g-5) = 5
    c: DistanceY(g0,g-5) = 1.15
FEATURE [PartDesign::Pad] Pad241
  BaseFeature = -> AdditiveLoft021
  Direction = (0,0,1)
  Length = 1.8
  Length2 = 10
  Placement = pos=(0,0,0) rot=(1,0,0;1.5708rad)
  Profile = -> Sketch374
  ReferenceAxis = -> Sketch374 [N_Axis]
  Refine = true
  Suppressed = false
  Type = 0
FEATURE [Sketcher::SketchObject] Sketch375
  ArcFitTolerance = 1e-06
  AttachmentSupport = -> [Pad241]
  ExternalGeometry = -> [Pad241]
  FullyConstrained = true
  MakeInternals = false
  MapMode = 5
  Placement = pos=(-15,0,0) rot=(0.707107,0,0.707107;3.14159rad)
  sketch-geometry (6):
    g0: LineSegment StartX=-33.5 StartY=1.15 StartZ=0 EndX=-31.7 EndY=1.5 EndZ=0
    g1: LineSegment StartX=-31.7 StartY=1.5 StartZ=0 EndX=-31.7 EndY=1.15 EndZ=0
    g2: LineSegment StartX=-31.7 StartY=1.15 StartZ=0 EndX=-33.5 EndY=1.15 EndZ=0
    g3: LineSegment StartX=-33.5 StartY=3.85 StartZ=0 EndX=-31.7 EndY=3.85 EndZ=0
    g4: LineSegment StartX=-31.7 StartY=3.85 StartZ=0 EndX=-31.7 EndY=3.5 EndZ=0
    g5: LineSegment StartX=-31.7 StartY=3.5 StartZ=0 EndX=-33.5 EndY=3.85 EndZ=0
  constraints (15):
    c: Coincident(g0,g-5)
    c: PointOnObject(g0,g-4)
    c: Coincident(g1,g0)
    c: Coincident(g1,g-5)
    c: Coincident(g2,g1)
    c: Coincident(g2,g0)
    c: Coincident(g3,g-3)
    c: Coincident(g3,g-4)
    c: Coincident(g4,g3)
    c: PointOnObject(g4,g-4)
    c: Coincident(g5,g4)
    c: Coincident(g5,g3)
    c: DistanceY(g0,g4) = 2
    c: DistanceY(g1,g3) = 2.7
    c: DistanceY(g4,g3) = 0.35
FEATURE [PartDesign::Pocket] Pocket069
  BaseFeature = -> Pad241
  Direction = (-1,0,2e-16)
  Length = 2.2
  Length2 = 5
  Placement = pos=(0,0,0) rot=(1,0,0;1.5708rad)
  Profile = -> Sketch375
  ReferenceAxis = -> Sketch375 [N_Axis]
  Refine = true
  Suppressed = false
  Type = 0
FEATURE [PartDesign::Pad] Pad242
  BaseFeature = -> Pocket069
  Direction = (-1,0,0)
  Length = 4.8
  Length2 = 10
  Placement = pos=(0,0,0) rot=(1,0,0;1.5708rad)
  Profile = -> Pocket069 [Face48]
  Refine = true
  Suppressed = false
  Type = 0
FEATURE [Sketcher::SketchObject] Sketch376
  ArcFitTolerance = 1e-06
  AttachmentSupport = -> [Pad242]
  ExternalGeometry = -> [Pad242]
  FullyConstrained = true
  MakeInternals = false
  MapMode = 5
  Placement = pos=(-15,0,0) rot=(0.707107,0,0.707107;3.14159rad)
  sketch-geometry (4):
    g0: LineSegment StartX=-33.5 StartY=3.85 StartZ=0 EndX=-33.5 EndY=1.15 EndZ=0
    g1: LineSegment StartX=-33.5 StartY=1.15 StartZ=0 EndX=-31.7 EndY=1.5 EndZ=0
    g2: LineSegment StartX=-31.7 StartY=1.5 StartZ=0 EndX=-31.7 EndY=3.5 EndZ=0
    g3: LineSegment StartX=-31.7 StartY=3.5 StartZ=0 EndX=-33.5 EndY=3.85 EndZ=0
  constraints (8):
    c: Coincident(g0,g-3)
    c: Coincident(g0,g-5)
    c: Coincident(g1,g0)
    c: Coincident(g1,g-5)
    c: Coincident(g2,g1)
    c: Coincident(g2,g-4)
    c: Coincident(g3,g2)
    c: Coincident(g3,g0)
FEATURE [PartDesign::Pocket] Pocket070
  BaseFeature = -> Pad242
  Direction = (-1,0,2e-16)
  Length = 4.8
  Length2 = 5
  Placement = pos=(0,0,0) rot=(1,0,0;1.5708rad)
  Profile = -> Sketch376
  ReferenceAxis = -> Sketch376 [N_Axis]
  Refine = true
  Suppressed = false
  Type = 0
FEATURE [PartDesign::Body] Body025  label="Scavanger_Gun"
  AllowCompound = false
  Group = -> [Sketch357,Pad234,Sketch358,Pocket060,Sketch359,Pocket061,Sketch360,Pad235,Sketch361,Pad236,Fillet046,Sketch362,Pocket062,Sketch363,Pocket063,Sketch364,Pocket064,Sketch365,Pocket065,Sketch366,Pocket066,Sketch367,Pocket067,Sketch368,Pocket068,Sketch369,Pad237,Pad238,Sketch370,Pad239,Sketch371,Pad240,Sketch372,Sketch373,AdditiveLoft021,Sketch374,Pad241,Sketch375,Pocket069,Pad242,Sketch376,Pocket070,+18 more]
  Origin = -> Origin027
  Placement = pos=(-19.9,-0.5,3.55) rot=(0,0,1;0rad)
  Tip = -> Pocket073
COMPONENT P9 — geometry summary ("Weapon_Stand"; its construction recipe is too large to include in this document):
  bounding box: 116.0 x 95.0 x 18.0 mm
  tessellated surface: 6,828 triangles
  volume: 16900 mm^3 (9% of its bounding box)
PROVENANCE & LICENSES
A FreeCAD (.FCStd) document from a public repository crawl; recipes are the document's own serialized feature recipes (and, for linked parts, companion documents' recipes).
License: as declared in the source repository (recorded in the dataset sidecar).
